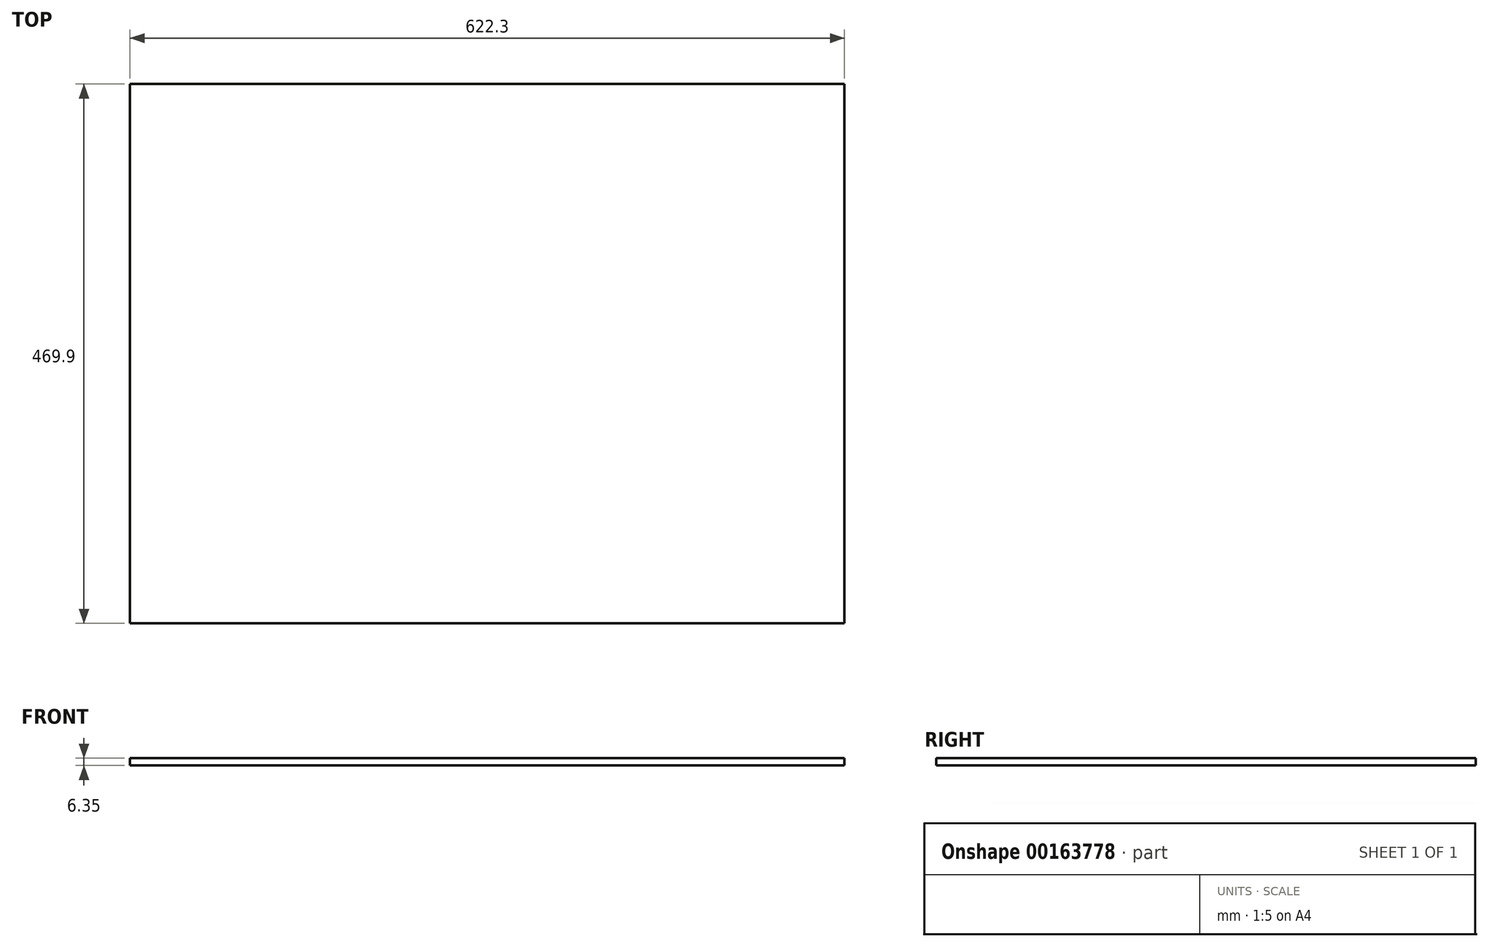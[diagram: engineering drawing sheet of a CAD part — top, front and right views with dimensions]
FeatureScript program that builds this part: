
annotation { "Feature Type Name" : "Feature", "Feature Type Description" : "" }
export const myFeature = defineFeature(function(context is Context, id is Id, definition is map)
    precondition{}
    {
        {
            var Q0;
            Q0=qCreatedBy(makeId("Top.planeOp"),FACE);
            var sketch = newSketch(context, id + "F0", { "sketchPlane" : qUnion([Q0])});
            skLineSegment(sketch, "E0.bottom", {"start": v(311.15, 234.95) * mm, "end": v(-311.15, 234.95) * mm});
            skLineSegment(sketch, "E0.top", {"start": v(311.15, -234.95) * mm, "end": v(-311.15, -234.95) * mm});
            skLineSegment(sketch, "E0.left", {"start": v(311.15, 234.95) * mm, "end": v(311.15, -234.95) * mm});
            skLineSegment(sketch, "E0.right", {"start": v(-311.15, 234.95) * mm, "end": v(-311.15, -234.95) * mm});
            skPoint(sketch, "E0.middle", {"position": v(0, 0) * mm});
            skSolve(sketch);
        }
        {
            var Q0;
            Q0=qSketchRegion(id+"F0",true);
            extrude(context, id + "F1", {"entities" : qUnion([Q0]), "depth" : 6.35 * mm});
        }
    });
